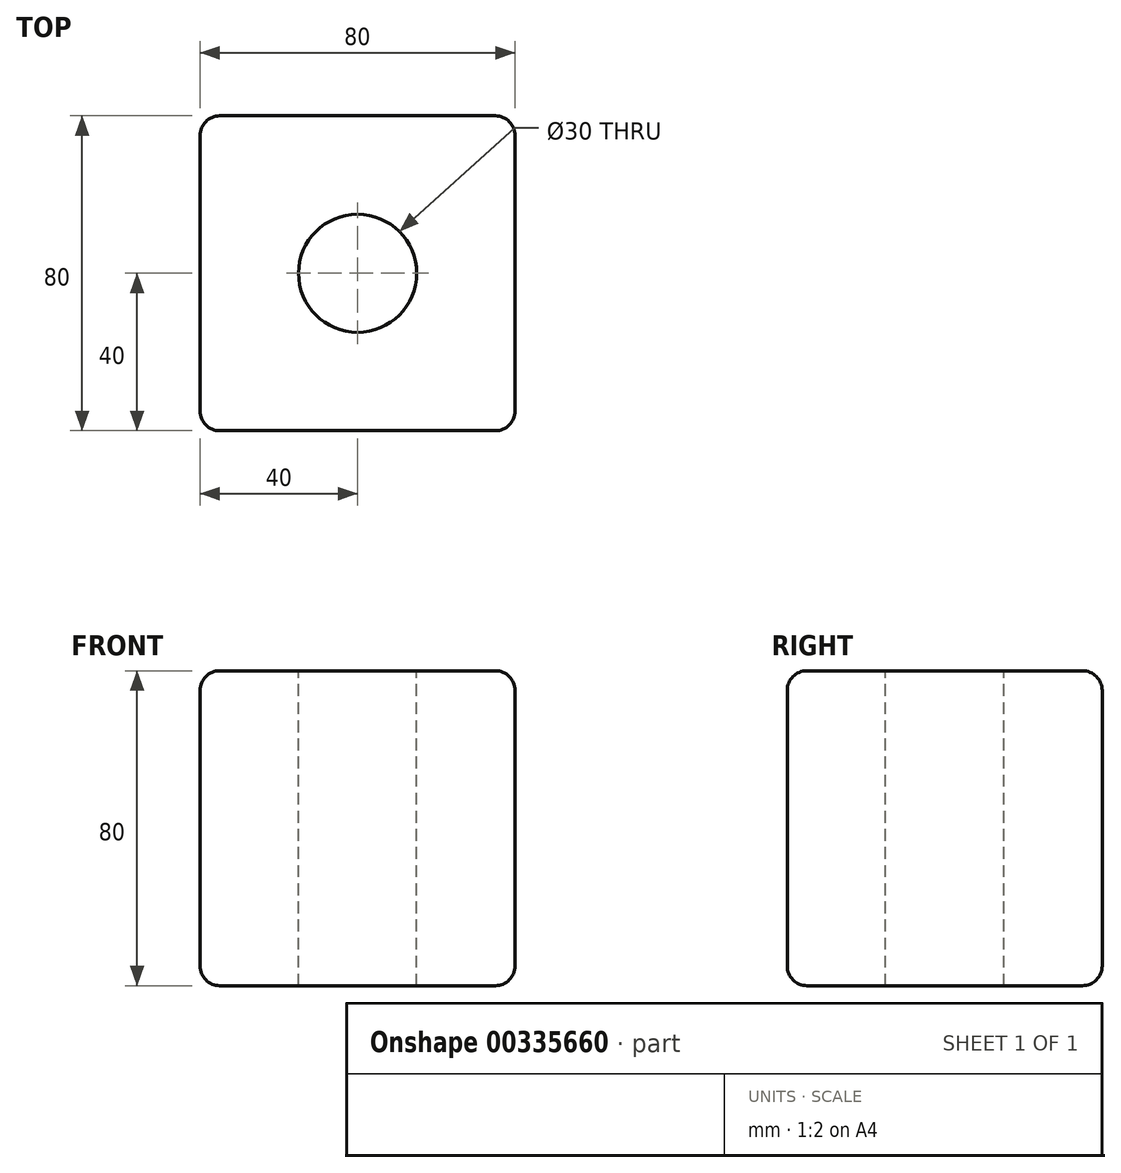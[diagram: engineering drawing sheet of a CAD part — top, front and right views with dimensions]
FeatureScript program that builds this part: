
annotation { "Feature Type Name" : "Feature", "Feature Type Description" : "" }
export const myFeature = defineFeature(function(context is Context, id is Id, definition is map)
    precondition{}
    {
        {
            var Q0;
            Q0=qCreatedBy(makeId("Top.planeOp"),FACE);
            var sketch = newSketch(context, id + "F0", { "sketchPlane" : qUnion([Q0])});
            skLineSegment(sketch, "E0.bottom", {"start": v(40, 40) * mm, "end": v(-40, 40) * mm});
            skLineSegment(sketch, "E0.top", {"start": v(40, -40) * mm, "end": v(-40, -40) * mm});
            skLineSegment(sketch, "E0.left", {"start": v(40, 40) * mm, "end": v(40, -40) * mm});
            skLineSegment(sketch, "E0.right", {"start": v(-40, 40) * mm, "end": v(-40, -40) * mm});
            skPoint(sketch, "E0.middle", {"position": v(0, 0) * mm});
            skSolve(sketch);
        }
        {
            var Q0;
            Q0=makeQuery(id+"F0.imprint","IMPRINT",FACE,{"disambiguationData":[TD([[makeQuery(id+"F0.imprint","IMPRINT",EDGE,{"derivedFrom":sQuery(id+"F0.wireOp",EDGE,"E0.bottom")}),1.0]])]});
            extrude(context, id + "F1", {"entities" : qUnion([Q0]), "endBound" : BoundingType.SYMMETRIC, "depth" : 80 * mm});
        }
        {
            var Q0;
            Q0=makeQuery(id+"F1.opExtrude","CAP_EDGE",EDGE,{"disambiguationData":[OSD([sQuery(id+"F0.wireOp",EDGE,"E0.bottom")])],"isStart":false});
            var Q1;
            Q1=makeQuery(id+"F1.opExtrude","CAP_EDGE",EDGE,{"disambiguationData":[OSD([sQuery(id+"F0.wireOp",EDGE,"E0.left")])],"isStart":false});
            var Q2;
            Q2=makeQuery(id+"F1.opExtrude","CAP_EDGE",EDGE,{"disambiguationData":[OSD([sQuery(id+"F0.wireOp",EDGE,"E0.top")])],"isStart":false});
            var Q3;
            Q3=makeQuery(id+"F1.opExtrude","CAP_EDGE",EDGE,{"disambiguationData":[OSD([sQuery(id+"F0.wireOp",EDGE,"E0.right")])],"isStart":true});
            var Q4;
            Q4=makeQuery(id+"F1.opExtrude","SWEPT_EDGE",EDGE,{"disambiguationData":[OSD([sQuery(id+"F0.wireOp",EDGE,"E0.bottom"),sQuery(id+"F0.wireOp",EDGE,"E0.right")])]});
            var Q5;
            Q5=makeQuery(id+"F1.opExtrude","SWEPT_EDGE",EDGE,{"disambiguationData":[OSD([sQuery(id+"F0.wireOp",EDGE,"E0.top"),sQuery(id+"F0.wireOp",EDGE,"E0.right")])]});
            var Q6;
            Q6=makeQuery(id+"F1.opExtrude","CAP_EDGE",EDGE,{"disambiguationData":[OSD([sQuery(id+"F0.wireOp",EDGE,"E0.right")])],"isStart":false});
            var Q7;
            Q7=makeQuery(id+"F1.opExtrude","CAP_EDGE",EDGE,{"disambiguationData":[OSD([sQuery(id+"F0.wireOp",EDGE,"E0.bottom")])],"isStart":true});
            var Q8;
            Q8=makeQuery(id+"F1.opExtrude","CAP_EDGE",EDGE,{"disambiguationData":[OSD([sQuery(id+"F0.wireOp",EDGE,"E0.left")])],"isStart":true});
            var Q9;
            Q9=makeQuery(id+"F1.opExtrude","CAP_EDGE",EDGE,{"disambiguationData":[OSD([sQuery(id+"F0.wireOp",EDGE,"E0.top")])],"isStart":true});
            var Q10;
            Q10=makeQuery(id+"F1.opExtrude","SWEPT_EDGE",EDGE,{"disambiguationData":[OSD([sQuery(id+"F0.wireOp",EDGE,"E0.bottom"),sQuery(id+"F0.wireOp",EDGE,"E0.left")])]});
            var Q11;
            Q11=makeQuery(id+"F1.opExtrude","SWEPT_EDGE",EDGE,{"disambiguationData":[OSD([sQuery(id+"F0.wireOp",EDGE,"E0.top"),sQuery(id+"F0.wireOp",EDGE,"E0.left")])]});
            fillet(context, id + "F2", {"entities" : qUnion([Q0, Q1, Q2, Q3, Q4, Q5, Q6, Q7, Q8, Q9, Q10, Q11]), "radius" : 5 * mm, "tangentPropagation" : true, "allowEdgeOverflow" : false});
        }
        {
            var Q0;
            Q0=makeQuery(id+"F1.opExtrude","CAP_FACE",FACE,{"disambiguationData":[OSD([sQuery(id+"F0.wireOp",EDGE,"E0.bottom"),sQuery(id+"F0.wireOp",EDGE,"E0.top"),sQuery(id+"F0.wireOp",EDGE,"E0.left"),sQuery(id+"F0.wireOp",EDGE,"E0.right")])],"isStart":false});
            var sketch = newSketch(context, id + "F3", { "sketchPlane" : qUnion([Q0])});
            skCircle(sketch, "E1", {"center": v(0, 0) * mm, "radius": 15 * mm});
            skSolve(sketch);
        }
        {
            var Q0;
            Q0=makeQuery(id+"F3.imprint","IMPRINT",FACE,{"disambiguationData":[TD([[makeQuery(id+"F3.imprint","IMPRINT",EDGE,{"derivedFrom":sQuery(id+"F3.wireOp",EDGE,"E1")}),1.0]])]});
            extrude(context, id + "F4", {"entities" : qUnion([Q0]), "operationType" : NewBodyOperationType.REMOVE, "endBound" : BoundingType.THROUGH_ALL, "oppositeDirection" : true, "depth" : 25 * mm});
        }
    });
